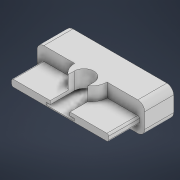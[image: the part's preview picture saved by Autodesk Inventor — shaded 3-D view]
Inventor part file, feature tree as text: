
AUTODESK INVENTOR PART (.ipt)
format: ipt  version: 2022 (Build 260153000, 153)  size: 484,864 bytes
history: native  units: mm
features: sketch x8, extrude x7, fillet x2, emboss x1
ambient origin geometry x8: Origin, YZ Plane, XZ Plane, XY Plane, X Axis, Y Axis, Z Axis, Center Point
bodies: Solid1 (feature_tree)
feature tree (18):
  extrude  "Extrusion1"  Depth=17.0mm
  emboss  "Emboss1"
  extrude  "Extrusion12"  Depth=1.0mm TaperAngle=0.0deg
  extrude  "Extrusion13"  Depth=8.0mm
  extrude  "Extrusion14"  Depth=18.0mm
  extrude  "Extrusion15"  Depth=2.0mm TaperAngle=0.0deg
  fillet  "Fillet6"  Radius=16.5mm
  fillet  "Fillet7"  Radius=1.4mm
  extrude  "Extrusion17"  Depth=18.0mm TaperAngle=0.0deg
  extrude  "Extrusion18"  Depth=4.0mm
  sketch  "Sketch1"  dims[d0=63.0mm d1=17.0mm]
  sketch  "Sketch10"  dims[d2=35.0mm d3=0.0mm d33=1.0mm d34=0.0mm]
  sketch  "Sketch15"  dims[d67=5.0mm d68=8.0mm]
  sketch  "Sketch16"  dims[d69=18.0mm d70=0.0mm d71=8.25mm]
  sketch  "Sketch17"  dims[d72=5.75mm d73=2.0mm d74=0.0mm d75=16.5mm d76=1.4mm d77=0.0mm]
  sketch  "Sketch18"  dims[d78=56.8mm d79=18.0mm d80=0.0mm]
  sketch  "Sketch20"  dims[d81=1.0mm d82=4.0mm]
  sketch  "Sketch21"  dims[d86=19.0mm d87=8.0mm d88=0.0mm d89=12.0mm d90=0.0mm d51=0.5mm d52=0.872665mm d53=0.5mm d54=0.872665mm d91=0.5mm d92=0.872665mm]
